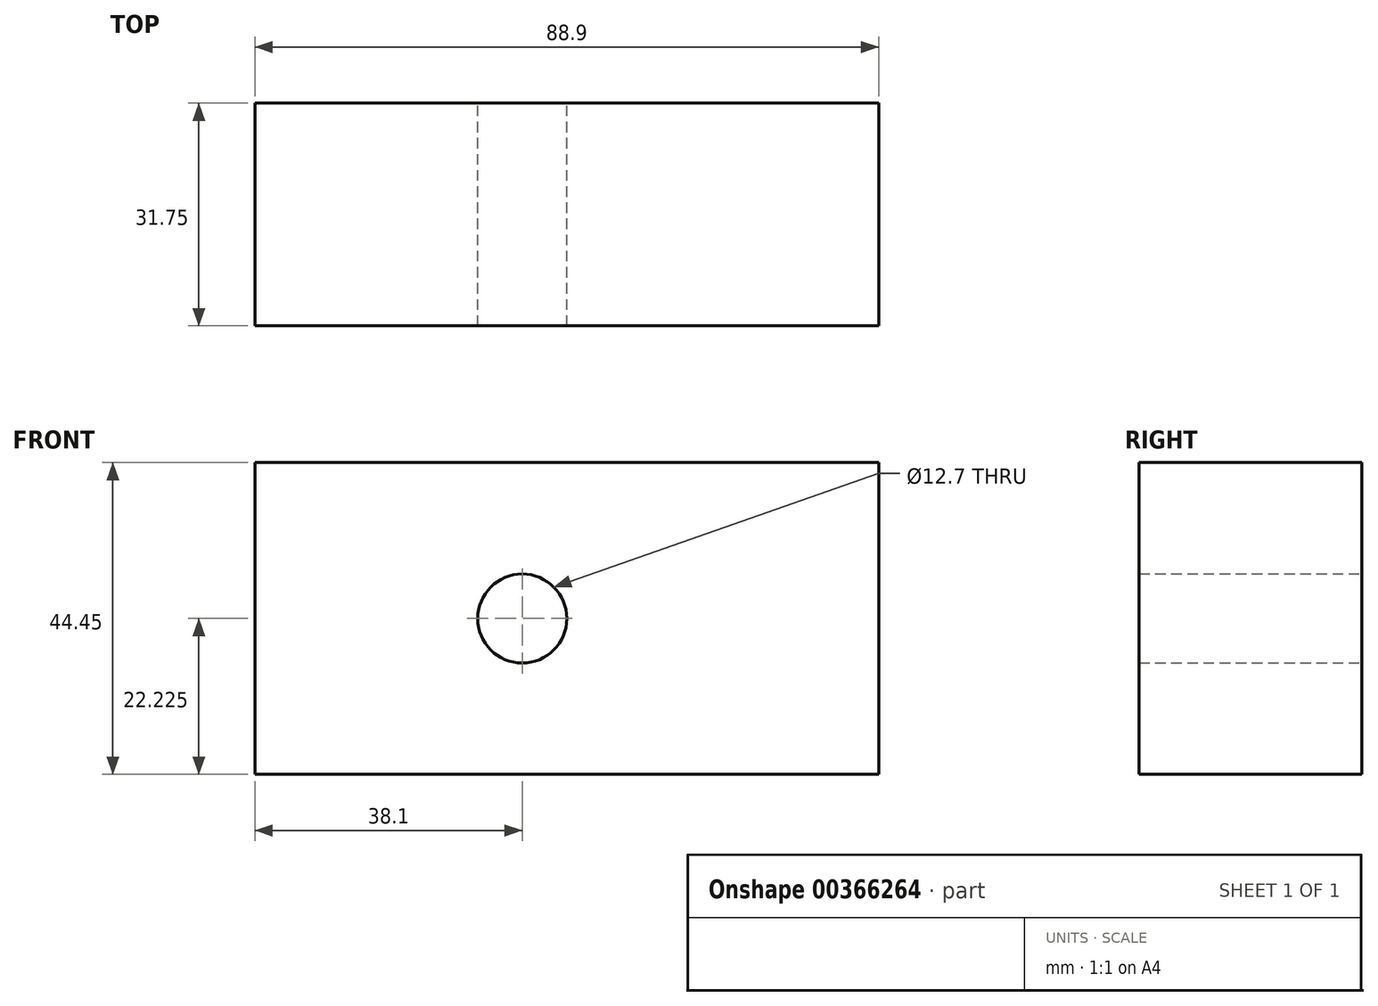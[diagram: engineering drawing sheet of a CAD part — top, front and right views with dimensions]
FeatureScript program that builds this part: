
annotation { "Feature Type Name" : "Feature", "Feature Type Description" : "" }
export const myFeature = defineFeature(function(context is Context, id is Id, definition is map)
    precondition{}
    {
        {
            var Q0;
            Q0=qCreatedBy(makeId("Front.planeOp"),FACE);
            var sketch = newSketch(context, id + "F0", { "sketchPlane" : qUnion([Q0])});
            skLineSegment(sketch, "E0", {"start": v(0, 0) * mm, "end": v(88.9, 0) * mm});
            skLineSegment(sketch, "E1", {"start": v(88.9, 0) * mm, "end": v(88.9, 44.45) * mm});
            skLineSegment(sketch, "E2", {"start": v(88.9, 44.45) * mm, "end": v(0, 44.45) * mm});
            skLineSegment(sketch, "E3", {"start": v(0, 44.45) * mm, "end": v(0, 0) * mm});
            skCircle(sketch, "E4", {"center": v(38.1, 22.22) * mm, "radius": 6.35 * mm});
            skSolve(sketch);
        }
        {
            var Q0;
            Q0=makeQuery(id+"F0.imprint","IMPRINT",FACE,{"disambiguationData":[TD([[makeQuery(id+"F0.imprint","IMPRINT",EDGE,{"derivedFrom":sQuery(id+"F0.wireOp",EDGE,"E0")}),1.0]])]});
            extrude(context, id + "F1", {"entities" : qUnion([Q0]), "depth" : 31.75 * mm});
        }
    });
